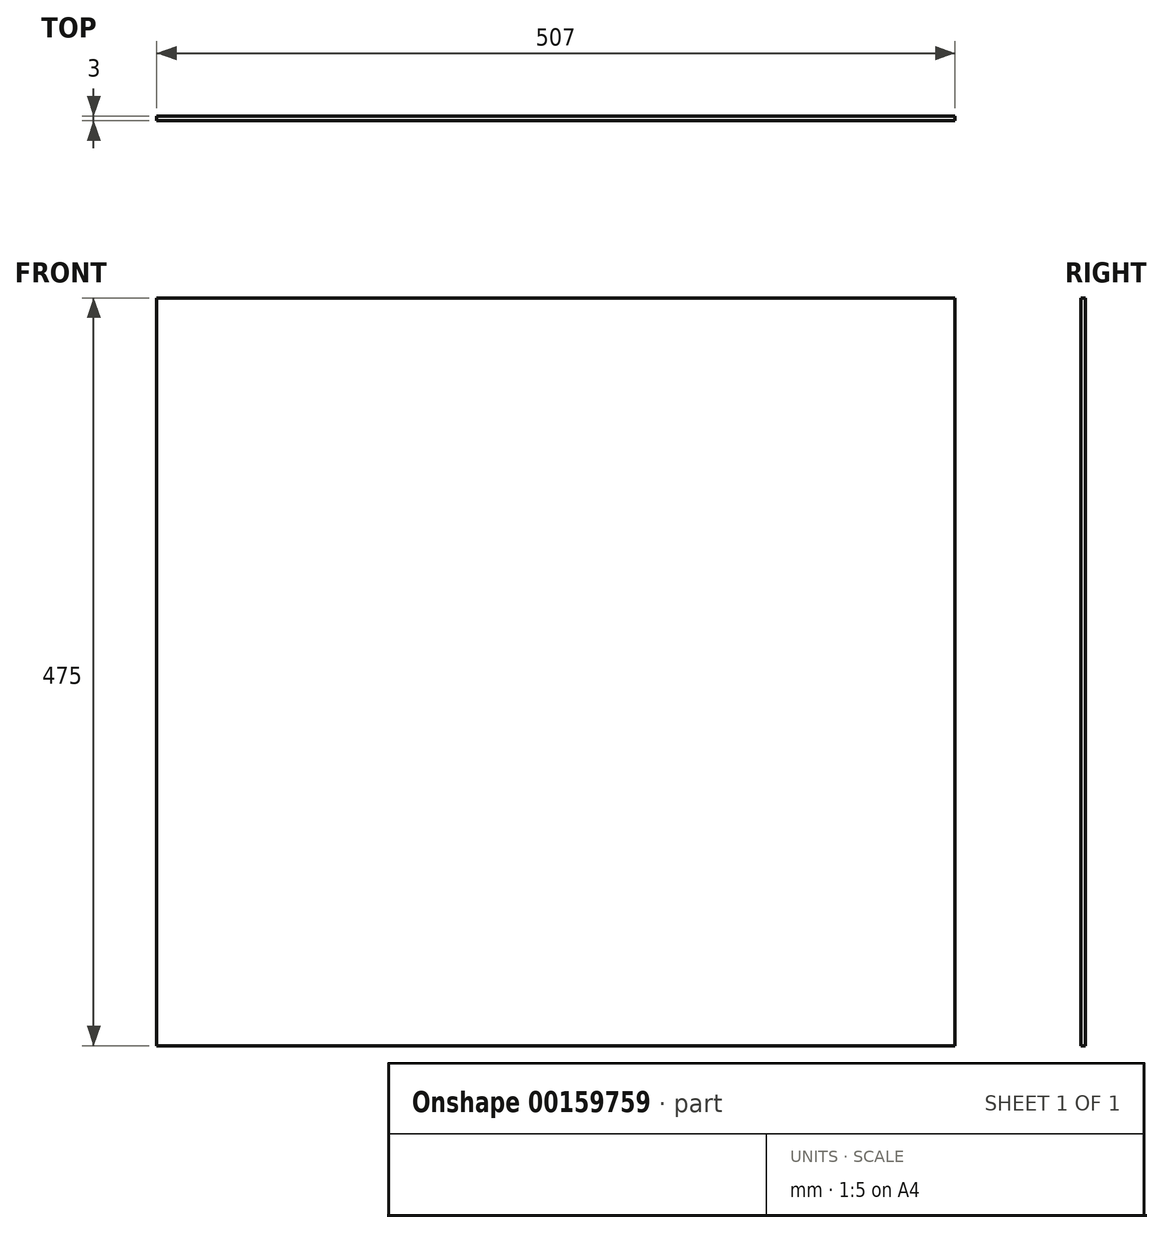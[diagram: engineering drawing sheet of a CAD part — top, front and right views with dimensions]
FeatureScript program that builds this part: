
annotation { "Feature Type Name" : "Feature", "Feature Type Description" : "" }
export const myFeature = defineFeature(function(context is Context, id is Id, definition is map)
    precondition{}
    {
        {
            var Q0;
            Q0=qCreatedBy(makeId("Front.planeOp"),FACE);
            var sketch = newSketch(context, id + "F0", { "sketchPlane" : qUnion([Q0])});
            skLineSegment(sketch, "E0.bottom", {"start": v(-220.36, 289) * mm, "end": v(286.64, 289) * mm});
            skLineSegment(sketch, "E0.top", {"start": v(-220.36, -186) * mm, "end": v(286.64, -186) * mm});
            skLineSegment(sketch, "E0.left", {"start": v(-220.36, 289) * mm, "end": v(-220.36, -186) * mm});
            skLineSegment(sketch, "E0.right", {"start": v(286.64, 289) * mm, "end": v(286.64, -186) * mm});
            skSolve(sketch);
        }
        {
            var Q0;
            Q0=makeQuery(id+"F0.imprint","IMPRINT",FACE,{"disambiguationData":[TD([[makeQuery(id+"F0.imprint","IMPRINT",EDGE,{"derivedFrom":sQuery(id+"F0.wireOp",EDGE,"E0.bottom")}),-1.0]])]});
            var Q1;
            Q1=sQuery(id+"F0.wireOp",EDGE,"E0.bottom");
            var Q2;
            Q2=sQuery(id+"F0.wireOp",EDGE,"E0.top");
            var Q3;
            Q3=sQuery(id+"F0.wireOp",EDGE,"E0.left");
            var Q4;
            Q4=sQuery(id+"F0.wireOp",EDGE,"E0.right");
            extrude(context, id + "F1", {"entities" : qUnion([Q0]), "surfaceEntities" : qUnion([Q1, Q2, Q3, Q4]), "depth" : 3 * mm});
        }
    });
